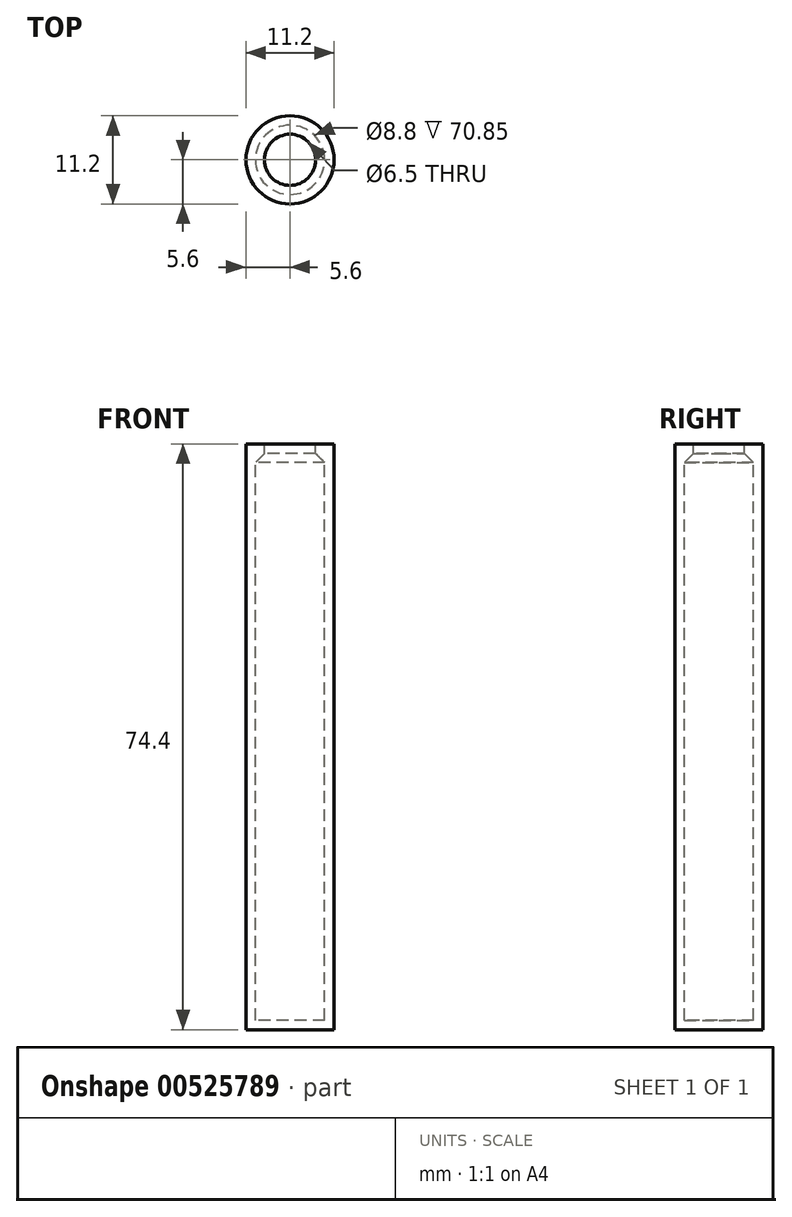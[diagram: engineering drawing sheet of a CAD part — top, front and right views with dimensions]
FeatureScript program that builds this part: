
annotation { "Feature Type Name" : "Feature", "Feature Type Description" : "" }
export const myFeature = defineFeature(function(context is Context, id is Id, definition is map)
    precondition{}
    {
        {
            var Q0;
            Q0=qCreatedBy(makeId("Front.planeOp"),FACE);
            var sketch = newSketch(context, id + "F0", { "sketchPlane" : qUnion([Q0])});
            skLineSegment(sketch, "E0", {"start": v(0, 1.2) * mm, "end": v(-4.4, 1.2) * mm});
            skLineSegment(sketch, "E1.0", {"start": v(-5.6, 74.4) * mm, "end": v(-3.25, 74.4) * mm});
            skLineSegment(sketch, "E1.1", {"start": v(-5.6, 0) * mm, "end": v(-5.6, 74.4) * mm});
            skLineSegment(sketch, "E1.2", {"start": v(0, 0) * mm, "end": v(-5.6, 0) * mm});
            skLineSegment(sketch, "E2", {"start": v(-3.25, 74.4) * mm, "end": v(-3.25, 73.2) * mm});
            skLineSegment(sketch, "E3", {"start": v(0, 1.2) * mm, "end": v(0, 0) * mm});
            skLineSegment(sketch, "E4", {"start": v(-3.25, 73.2) * mm, "end": v(-4.4, 72.05) * mm});
            skLineSegment(sketch, "E5", {"start": v(-4.4, 72.05) * mm, "end": v(-4.4, 1.2) * mm});
            skLineSegment(sketch, "E6", {"start": v(-3.25, 73.2) * mm, "end": v(-8.99, 73.2) * mm, "construction": true});
            skSolve(sketch);
        }
        {
            var Q0;
            Q0=makeQuery(id+"F0.imprint","IMPRINT",FACE,{"disambiguationData":[TD([[makeQuery(id+"F0.imprint","IMPRINT",EDGE,{"derivedFrom":sQuery(id+"F0.wireOp",EDGE,"E0")}),1.0]])]});
            var Q1;
            Q1=sQuery(id+"F0.wireOp",EDGE,"E3");
            revolve(context, id + "F1", {"entities" : qUnion([Q0]), "axis" : qUnion([Q1]), "revolveType" : RevolveType.FULL});
        }
    });
